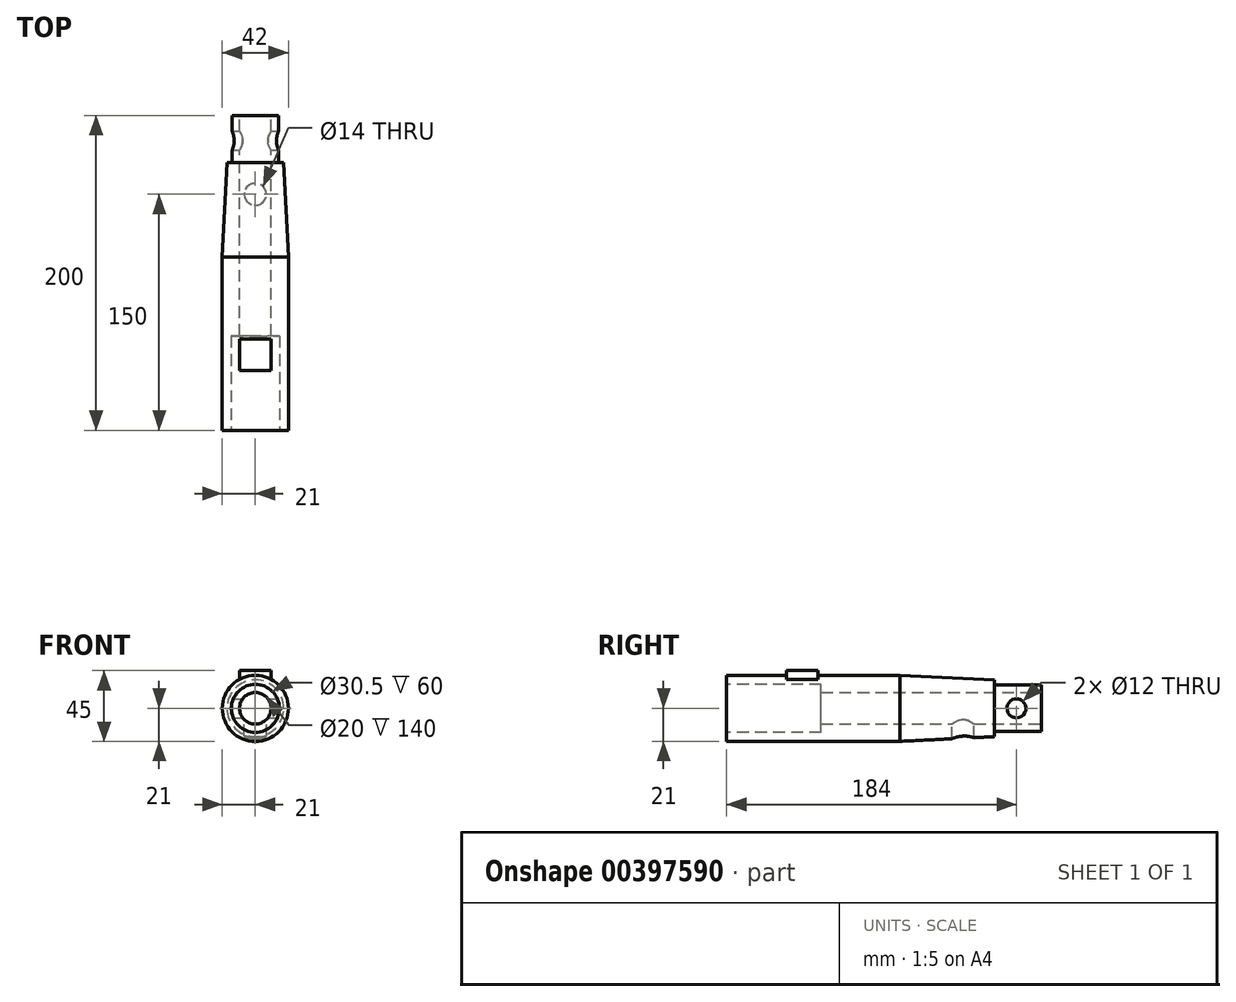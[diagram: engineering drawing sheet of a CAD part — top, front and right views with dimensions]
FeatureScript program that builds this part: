
annotation { "Feature Type Name" : "Feature", "Feature Type Description" : "" }
export const myFeature = defineFeature(function(context is Context, id is Id, definition is map)
    precondition{}
    {
        {
            var Q0;
            Q0=qCreatedBy(makeId("Front.planeOp"),FACE);
            var sketch = newSketch(context, id + "F0", { "sketchPlane" : qUnion([Q0])});
            skCircle(sketch, "E0", {"center": v(0, 0) * mm, "radius": 21 * mm});
            skSolve(sketch);
        }
        {
            var Q0;
            Q0=qSketchRegion(id+"F0",true);
            extrude(context, id + "F1", {"entities" : qUnion([Q0]), "depth" : 170 * mm});
        }
        {
            var Q0;
            Q0=makeQuery(id+"F1.opExtrude","CAP_FACE",FACE,{"disambiguationData":[OSD([sQuery(id+"F0.wireOp",EDGE,"E0")])],"isStart":false});
            var sketch = newSketch(context, id + "F2", { "sketchPlane" : qUnion([Q0])});
            skCircle(sketch, "E1", {"center": v(0, 0) * mm, "radius": 15.25 * mm});
            skSolve(sketch);
        }
        {
            var Q0;
            Q0=makeQuery(id+"F2.imprint","IMPRINT",FACE,{"disambiguationData":[TD([[makeQuery(id+"F2.imprint","IMPRINT",EDGE,{"derivedFrom":sQuery(id+"F2.wireOp",EDGE,"E1")}),1.0]])]});
            extrude(context, id + "F3", {"entities" : qUnion([Q0]), "operationType" : NewBodyOperationType.REMOVE, "oppositeDirection" : true, "depth" : 25 * mm});
        }
        {
            var Q0;
            Q0=makeQuery(id+"F1.opExtrude","CAP_FACE",FACE,{"disambiguationData":[OSD([sQuery(id+"F0.wireOp",EDGE,"E0")])],"isStart":true});
            var sketch = newSketch(context, id + "F4", { "sketchPlane" : qUnion([Q0])});
            skCircle(sketch, "E2", {"center": v(0, 0) * mm, "radius": 14.75 * mm});
            skSolve(sketch);
        }
        {
            var Q0;
            Q0=makeQuery(id+"F4.imprint","IMPRINT",FACE,{"disambiguationData":[TD([[makeQuery(id+"F4.imprint","IMPRINT",EDGE,{"derivedFrom":sQuery(id+"F4.wireOp",EDGE,"E2")}),1.0]])]});
            extrude(context, id + "F5", {"entities" : qUnion([Q0]), "operationType" : NewBodyOperationType.ADD, "depth" : 30 * mm});
        }
        {
            var Q0;
            Q0=qCreatedBy(makeId("Top.planeOp"),FACE);
            var sketch = newSketch(context, id + "F6", { "sketchPlane" : qUnion([Q0])});
            skLineSegment(sketch, "E3", {"start": v(0, 0) * mm, "end": v(0, -20) * mm});
            skCircle(sketch, "E4", {"center": v(0, -20) * mm, "radius": 7 * mm});
            skSolve(sketch);
        }
        {
            var Q0;
            Q0=qSketchRegion(id+"F6",true);
            extrude(context, id + "F7", {"entities" : qUnion([Q0]), "operationType" : NewBodyOperationType.REMOVE, "oppositeDirection" : true, "depth" : 32.4 * mm});
        }
        {
            var Q0;
            Q0=makeQuery(id+"F1.opExtrude","CAP_EDGE",EDGE,{"disambiguationData":[OSD([sQuery(id+"F0.wireOp",EDGE,"E0")])],"isStart":true});
            chamfer(context, id + "F8", {"entities" : qUnion([Q0]), "chamferType" : ChamferType.TWO_OFFSETS, "width1" : 60 * mm, "oppositeDirection" : false, "width2" : 3 * mm, "tangentPropagation" : true});
        }
        {
            var Q0;
            Q0=qCreatedBy(makeId("Top.planeOp"),FACE);
            var sketch = newSketch(context, id + "F9", { "sketchPlane" : qUnion([Q0])});
            skLineSegment(sketch, "E5", {"start": v(0, 0) * mm, "end": v(0, -122) * mm});
            skLineSegment(sketch, "E6.bottom", {"start": v(-10, -112) * mm, "end": v(10, -112) * mm});
            skLineSegment(sketch, "E6.top", {"start": v(-10, -132) * mm, "end": v(10, -132) * mm});
            skLineSegment(sketch, "E6.left", {"start": v(-10, -112) * mm, "end": v(-10, -132) * mm});
            skLineSegment(sketch, "E6.right", {"start": v(10, -112) * mm, "end": v(10, -132) * mm});
            skPoint(sketch, "E6.middle", {"position": v(0, -122) * mm});
            skLineSegment(sketch, "E7", {"start": v(0, -59.93) * mm, "end": v(0, -170) * mm});
            skSolve(sketch);
        }
        {
            var Q0;
            Q0=qSketchRegion(id+"F9",true);
            extrude(context, id + "F10", {"entities" : qUnion([Q0]), "operationType" : NewBodyOperationType.ADD, "depth" : 24 * mm});
        }
        {
            var Q0;
            Q0=makeQuery(id+"F1.opExtrude","CAP_FACE",FACE,{"disambiguationData":[OSD([sQuery(id+"F0.wireOp",EDGE,"E0")])],"isStart":false});
            var sketch = newSketch(context, id + "F11", { "sketchPlane" : qUnion([Q0])});
            skCircle(sketch, "E8", {"center": v(0, 0) * mm, "radius": 15.25 * mm});
            skSolve(sketch);
        }
        {
            var Q0;
            Q0=qSketchRegion(id+"F11",true);
            extrude(context, id + "F12", {"entities" : qUnion([Q0]), "operationType" : NewBodyOperationType.REMOVE, "oppositeDirection" : true, "depth" : 60 * mm});
        }
        {
            var Q0;
            Q0=makeQuery(id+"F5.opExtrude","CAP_FACE",FACE,{"disambiguationData":[OSD([sQuery(id+"F4.wireOp",EDGE,"E2")])],"isStart":false});
            var sketch = newSketch(context, id + "F13", { "sketchPlane" : qUnion([Q0])});
            skCircle(sketch, "E9", {"center": v(0, 0) * mm, "radius": 10 * mm});
            skSolve(sketch);
        }
        {
            var Q0;
            Q0=qSketchRegion(id+"F13",true);
            extrude(context, id + "F14", {"entities" : qUnion([Q0]), "operationType" : NewBodyOperationType.REMOVE, "oppositeDirection" : true, "depth" : 207 * mm});
        }
        {
            var Q0;
            Q0=qCreatedBy(makeId("Right.planeOp"),FACE);
            cPlane(context, id + "F15", {"entities" : qUnion([Q0]), "cplaneType" : CPlaneType.OFFSET, "offset" : 25 * mm, "width" : 150 * mm, "height" : 150 * mm});
        }
        {
            var Q0;
            Q0=qCreatedBy(id+"F15.planeOp",FACE);
            var sketch = newSketch(context, id + "F16", { "sketchPlane" : qUnion([Q0])});
            skLineSegment(sketch, "E10", {"start": v(0, 0) * mm, "end": v(14, 0) * mm});
            skCircle(sketch, "E11", {"center": v(14, 0) * mm, "radius": 6 * mm});
            skSolve(sketch);
        }
        {
            var Q0;
            Q0=qSketchRegion(id+"F16",true);
            extrude(context, id + "F17", {"entities" : qUnion([Q0]), "operationType" : NewBodyOperationType.REMOVE, "oppositeDirection" : true, "depth" : 45.8 * mm});
        }
    });
